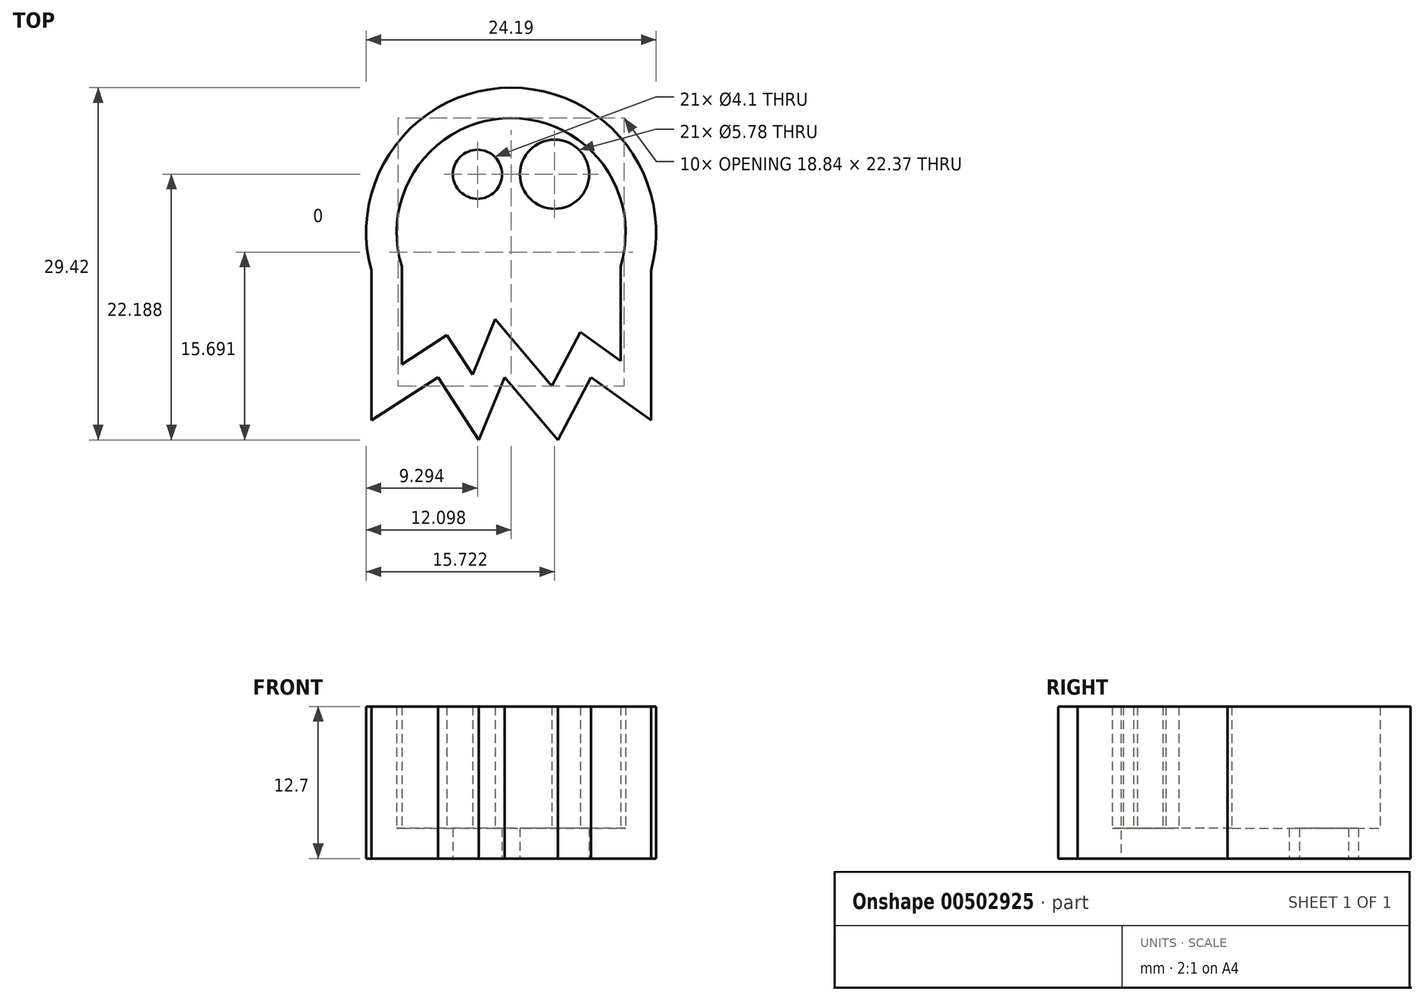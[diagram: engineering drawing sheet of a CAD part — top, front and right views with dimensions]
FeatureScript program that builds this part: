
annotation { "Feature Type Name" : "Feature", "Feature Type Description" : "" }
export const myFeature = defineFeature(function(context is Context, id is Id, definition is map)
    precondition{}
    {
        {
            var Q0;
            Q0=qCreatedBy(makeId("Top.planeOp"),FACE);
            var sketch = newSketch(context, id + "F0", { "sketchPlane" : qUnion([Q0])});
            skArc(sketch, "E0", {"start": v(23.34, 0) * mm, "mid": v(11.67, 15.28) * mm, "end": v(0, 0) * mm});
            skLineSegment(sketch, "E1", {"start": v(0, 0) * mm, "end": v(0, -12.5) * mm});
            skLineSegment(sketch, "E2", {"start": v(23.34, 0) * mm, "end": v(23.34, -12.5) * mm});
            skLineSegment(sketch, "E3", {"start": v(0, -12.5) * mm, "end": v(5.56, -8.9) * mm});
            skLineSegment(sketch, "E4", {"start": v(5.56, -8.9) * mm, "end": v(8.96, -14.14) * mm});
            skLineSegment(sketch, "E5", {"start": v(8.96, -14.14) * mm, "end": v(11.11, -8.9) * mm});
            skLineSegment(sketch, "E6", {"start": v(11.11, -8.9) * mm, "end": v(15.56, -14.14) * mm});
            skLineSegment(sketch, "E7", {"start": v(15.56, -14.14) * mm, "end": v(18.34, -8.9) * mm});
            skLineSegment(sketch, "E8", {"start": v(18.34, -8.9) * mm, "end": v(23.34, -12.5) * mm});
            skCircle(sketch, "E9", {"center": v(4.44, 4.16) * mm, "radius": 2.74 * mm});
            skCircle(sketch, "E10", {"center": v(15.56, 4.72) * mm, "radius": 5.96 * mm});
            skSolve(sketch);
        }
        {
            var Q0;
            Q0=makeQuery(id+"F0.imprint","IMPRINT",FACE,{"disambiguationData":[TD([[makeQuery(id+"F0.imprint","IMPRINT",EDGE,{"derivedFrom":sQuery(id+"F0.wireOp",EDGE,"E10")}),1.0]])]});
            var Q1;
            Q1=makeQuery(id+"F0.imprint","IMPRINT",FACE,{"disambiguationData":[TD([[makeQuery(id+"F0.imprint","IMPRINT",EDGE,{"derivedFrom":sQuery(id+"F0.wireOp",EDGE,"E9")}),1.0]])]});
            var Q2;
            Q2=makeQuery(id+"F0.imprint","IMPRINT",FACE,{"disambiguationData":[TD([[makeQuery(id+"F0.imprint","IMPRINT",EDGE,{"derivedFrom":sQuery(id+"F0.wireOp",EDGE,"E0")}),1.0]])]});
            extrude(context, id + "F1", {"entities" : qUnion([Q0, Q1, Q2]), "depth" : 12.7 * mm, "offsetDistance" : 25.4 * mm});
        }
        {
            var Q0;
            Q0=qCreatedBy(makeId("Top.planeOp"),FACE);
            var sketch = newSketch(context, id + "F2", { "sketchPlane" : qUnion([Q0])});
            skCircle(sketch, "E11", {"center": v(15.3, 8.05) * mm, "radius": 2.89 * mm});
            skCircle(sketch, "E12", {"center": v(8.86, 8.05) * mm, "radius": 2.05 * mm});
            skSolve(sketch);
        }
        {
            var Q0;
            Q0=makeQuery(id+"F1.opExtrude","CAP_FACE",FACE,{"disambiguationData":[OSD([sQuery(id+"F0.wireOp",EDGE,"E0"),sQuery(id+"F0.wireOp",EDGE,"E1"),sQuery(id+"F0.wireOp",EDGE,"E2"),sQuery(id+"F0.wireOp",EDGE,"E3"),sQuery(id+"F0.wireOp",EDGE,"E4"),sQuery(id+"F0.wireOp",EDGE,"E5"),sQuery(id+"F0.wireOp",EDGE,"E6"),sQuery(id+"F0.wireOp",EDGE,"E7"),sQuery(id+"F0.wireOp",EDGE,"E8")])],"isStart":false});
            shell(context, id + "F3", {"entities" : qUnion([Q0]), "thickness" : 2.54 * mm});
        }
        {
            var Q0;
            Q0 = qSketchRegion(id + "F2", true);
            extrude(context, id + "F4", {"entities" : qUnion([Q0]), "operationType" : NewBodyOperationType.REMOVE, "depth" : 61.98 * mm, "offsetDistance" : 25.4 * mm});
        }
    });
